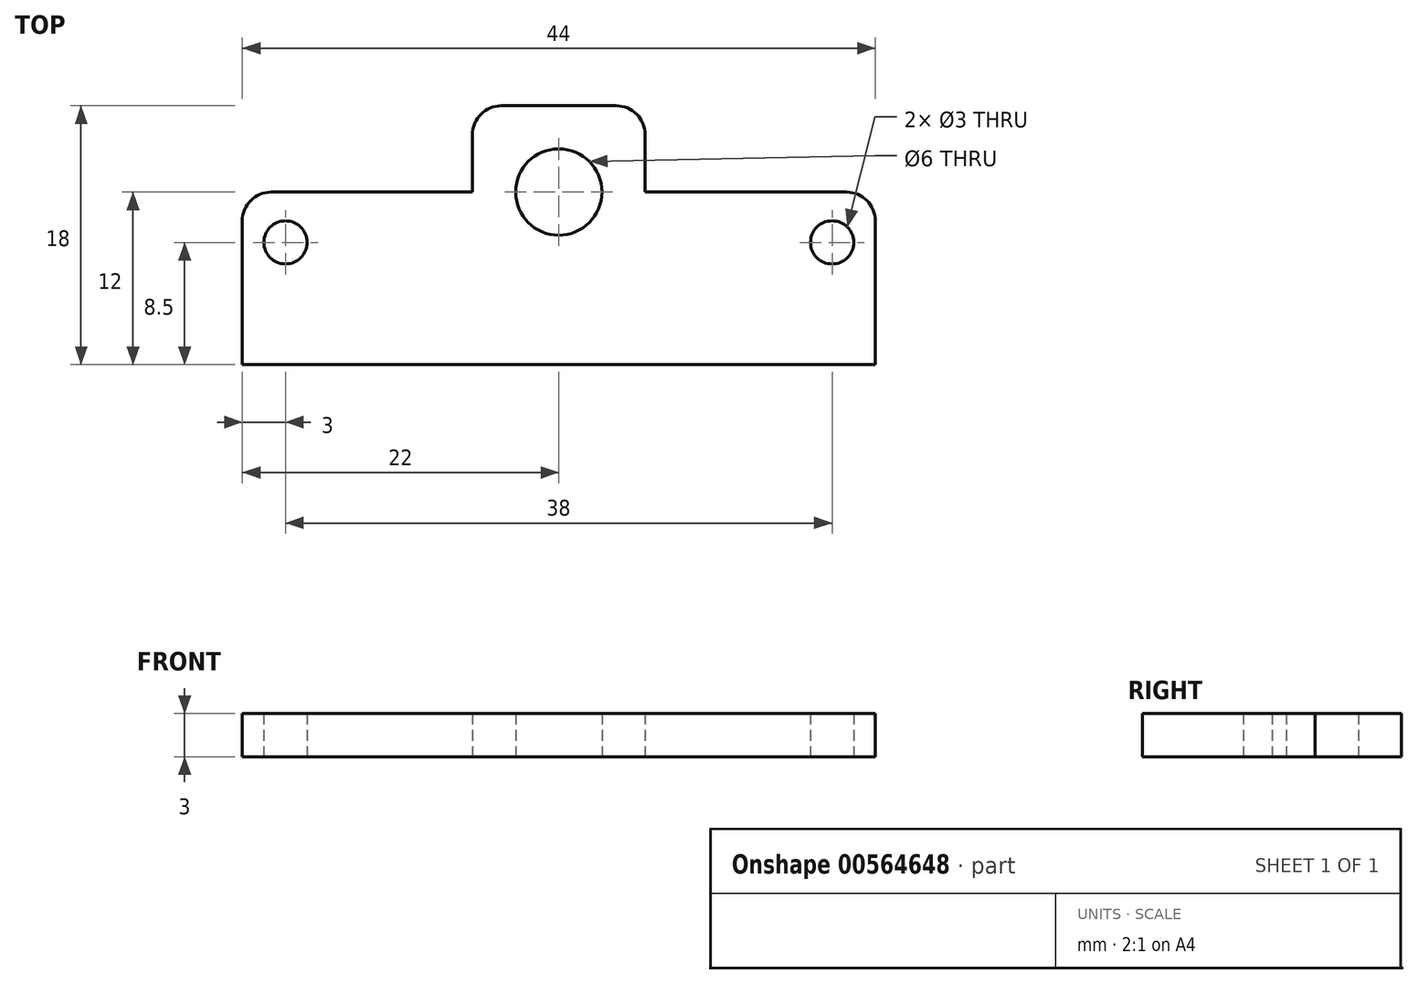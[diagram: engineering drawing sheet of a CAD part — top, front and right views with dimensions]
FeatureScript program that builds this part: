
annotation { "Feature Type Name" : "Feature", "Feature Type Description" : "" }
export const myFeature = defineFeature(function(context is Context, id is Id, definition is map)
    precondition{}
    {
        {
            var Q0;
            Q0=qCreatedBy(makeId("Top.planeOp"),FACE);
            var sketch = newSketch(context, id + "F0", { "sketchPlane" : qUnion([Q0])});
            skLineSegment(sketch, "E0.bottom", {"start": v(0, 0) * mm, "end": v(44, 0) * mm});
            skLineSegment(sketch, "E0.top", {"start": v(0, 12) * mm, "end": v(16, 12) * mm});
            skLineSegment(sketch, "E0.left", {"start": v(0, 0) * mm, "end": v(0, 12) * mm});
            skLineSegment(sketch, "E0.right", {"start": v(44, 0) * mm, "end": v(44, 12) * mm});
            skLineSegment(sketch, "E1", {"start": v(22, 24.8) * mm, "end": v(22, -5.1) * mm, "construction": true});
            skPoint(sketch, "E1.startSnap0", {"position": v(22, 12) * mm});
            skLineSegment(sketch, "E2.top", {"start": v(16, 18) * mm, "end": v(28, 18) * mm});
            skLineSegment(sketch, "E2.left", {"start": v(16, 12) * mm, "end": v(16, 18) * mm});
            skLineSegment(sketch, "E2.right", {"start": v(28, 12) * mm, "end": v(28, 18) * mm});
            skLineSegment(sketch, "E3.trimOffspring", {"start": v(28, 12) * mm, "end": v(44, 12) * mm});
            skLineSegment(sketch, "E4", {"start": v(3, 24.03) * mm, "end": v(3, -4.85) * mm, "construction": true});
            skLineSegment(sketch, "E5", {"start": v(41, 24.2) * mm, "end": v(41, -4.85) * mm, "construction": true});
            skLineSegment(sketch, "E6", {"start": v(-15.18, 8.5) * mm, "end": v(49.5, 8.5) * mm, "construction": true});
            skPoint(sketch, "E7", {"position": v(41, 8.5) * mm});
            skPoint(sketch, "E8", {"position": v(3, 8.5) * mm});
            skSolve(sketch);
        }
        {
            var Q0;
            Q0=makeQuery(id+"F0.imprint","IMPRINT",FACE,{"disambiguationData":[TD([[makeQuery(id+"F0.imprint","IMPRINT",EDGE,{"derivedFrom":sQuery(id+"F0.wireOp",EDGE,"E0.bottom")}),1.0]])]});
            extrude(context, id + "F1", {"entities" : qUnion([Q0]), "depth" : 3 * mm, "offsetDistance" : 25 * mm});
        }
        {
            var Q0;
            Q0=sQuery(id+"F0.wireOp",VERTEX,"E1.startSnap0");
            var Q1;
            Q1=makeQuery(id+"F1.opExtrude","SWEPT_BODY",BODY,{"disambiguationData":[OSD([sQuery(id+"F0.wireOp",EDGE,"E0.bottom"),sQuery(id+"F0.wireOp",EDGE,"E0.top"),sQuery(id+"F0.wireOp",EDGE,"E0.left"),sQuery(id+"F0.wireOp",EDGE,"E0.right"),sQuery(id+"F0.wireOp",EDGE,"E2.top"),sQuery(id+"F0.wireOp",EDGE,"E2.left"),sQuery(id+"F0.wireOp",EDGE,"E2.right"),sQuery(id+"F0.wireOp",EDGE,"E3.trimOffspring")])]});
            hole(context, id + "F2", {"style" : HoleStyle.SIMPLE, "endStyle" : HoleEndStyle.THROUGH, "oppositeDirection" : true, "holeDiameter" : 6 * mm, "isTappedThrough" : true, "tappedDepth" : 12 * mm, "tapClearance" : 3, "locations" : qUnion([Q0]), "scope" : qUnion([Q1])});
        }
        {
            var Q0;
            Q0=sQuery(id+"F0.wireOp",VERTEX,"E8");
            var Q1;
            Q1=sQuery(id+"F0.wireOp",VERTEX,"E7");
            var Q2;
            Q2=makeQuery(id+"F1.opExtrude","SWEPT_BODY",BODY,{"disambiguationData":[OSD([sQuery(id+"F0.wireOp",EDGE,"E0.bottom"),sQuery(id+"F0.wireOp",EDGE,"E0.top"),sQuery(id+"F0.wireOp",EDGE,"E0.left"),sQuery(id+"F0.wireOp",EDGE,"E0.right"),sQuery(id+"F0.wireOp",EDGE,"E2.top"),sQuery(id+"F0.wireOp",EDGE,"E2.left"),sQuery(id+"F0.wireOp",EDGE,"E2.right"),sQuery(id+"F0.wireOp",EDGE,"E3.trimOffspring")])]});
            hole(context, id + "F3", {"style" : HoleStyle.SIMPLE, "endStyle" : HoleEndStyle.THROUGH, "oppositeDirection" : true, "holeDiameter" : 3 * mm, "isTappedThrough" : true, "tappedDepth" : 12 * mm, "tapClearance" : 3, "locations" : qUnion([Q0, Q1]), "scope" : qUnion([Q2])});
        }
        {
            var Q0;
            Q0=makeQuery(id+"F1.opExtrude","SWEPT_EDGE",EDGE,{"disambiguationData":[OSD([sQuery(id+"F0.wireOp",EDGE,"E2.top"),sQuery(id+"F0.wireOp",EDGE,"E2.right")])]});
            var Q1;
            Q1=makeQuery(id+"F1.opExtrude","SWEPT_EDGE",EDGE,{"disambiguationData":[OSD([sQuery(id+"F0.wireOp",EDGE,"E2.top"),sQuery(id+"F0.wireOp",EDGE,"E2.left")])]});
            var Q2;
            Q2=makeQuery(id+"F1.opExtrude","SWEPT_EDGE",EDGE,{"disambiguationData":[OSD([sQuery(id+"F0.wireOp",EDGE,"E0.right"),sQuery(id+"F0.wireOp",EDGE,"E3.trimOffspring")])]});
            var Q3;
            Q3=makeQuery(id+"F1.opExtrude","SWEPT_EDGE",EDGE,{"disambiguationData":[OSD([sQuery(id+"F0.wireOp",EDGE,"E0.top"),sQuery(id+"F0.wireOp",EDGE,"E0.left")])]});
            fillet(context, id + "F4", {"entities" : qUnion([Q0, Q1, Q2, Q3]), "radius" : 2 * mm, "tangentPropagation" : true, "allowEdgeOverflow" : false});
        }
    });
